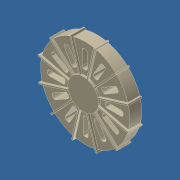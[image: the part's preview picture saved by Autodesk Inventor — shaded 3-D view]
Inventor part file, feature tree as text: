
AUTODESK INVENTOR PART (.ipt)
format: ipt  version: unknown  size: 766,464 bytes
history: native  units: in
note: dims shown in document units (in); Inventor stores cm internally (conversion verified against a paired STEP export)
features: extrude x10, sketch x10, pattern_circular x4, projected_geometry x1
ambient origin geometry x8: Origin, YZ Plane, XZ Plane, XY Plane, X Axis, Y Axis, Z Axis, Center Point
bodies: Solid1 (feature_tree)
feature tree (25):
  extrude  "Extrusion1"  Depth=3.15in
  extrude  "Extrusion2"  Depth=3.0in
  extrude  "Extrusion3"  Depth=3.375in TaperAngle=0.0deg
  extrude  "Extrusion4"  Depth=1.15in
  extrude  "Extrusion5"  Depth=0.05in
  pattern_circular  "Circular Pattern1"  Count=12 Angle=360.0deg
  extrude  "Extrusion6"  Depth=4.7244in TaperAngle=360.0deg
  pattern_circular  "Circular Pattern2"  [2 undecoded]
  extrude  "Extrusion7"  Depth=0.075in
  pattern_circular  "Circular Pattern3"  [2 undecoded]
  extrude  "Extrusion8"  Depth=4.7244in TaperAngle=360.0deg
  pattern_circular  "Circular Pattern4"  [2 undecoded]
  extrude  "Extrusion9"  Depth=0.075in
  extrude  "Extrusion10"  Depth=0.15in TaperAngle=0.0deg
  sketch  "Sketch1"  dims[d0=3.35in d1=3.15in]
  sketch  "Sketch2"  dims[d2=3.375in d3=0.0in d4=3.0in]
  sketch  "Sketch3"  dims[d5=0.125in d6=0.0in d7=3.375in d8=0.0in]
  sketch  "Sketch4"  dims[d9=0.45in d10=0.0in d11=1.15in]
  sketch  "Sketch5"  dims[d13=0.05in d15=0.05in]
  sketch  "Sketch6"  dims[d16=0.05in d18=4.7244in d20=360.0deg]
  sketch  "Sketch7"  dims[d22=0.075in d23=0.0in d24=4.7244in d25=360.0deg]
  projected_geometry  "Projected Loop1"
  sketch  "Sketch8"  dims[d27=0.1168in]
  sketch  "Sketch9"  dims[d28=0.675in]
  sketch  "Sketch10"  dims[d29=0.2in d30=0.25in d31=0.075in d32=0.45in d33=0.0in d34=4.7244in d35=360.0deg d38=0.075in d39=0.075in d40=0.15in d41=0.0in d42=4.7244in d43=360.0deg d45=3.7in d46=0.0in d47=4.7244in d48=360.0deg d50=0.07in d51=0.0in d52=1.0in d53=0.0in]
note: 6 required parameter values undecoded (feature->parameter linkage not recoverable at this tier; creation-order binding heuristic only, values carry confidence <= 0.55)
